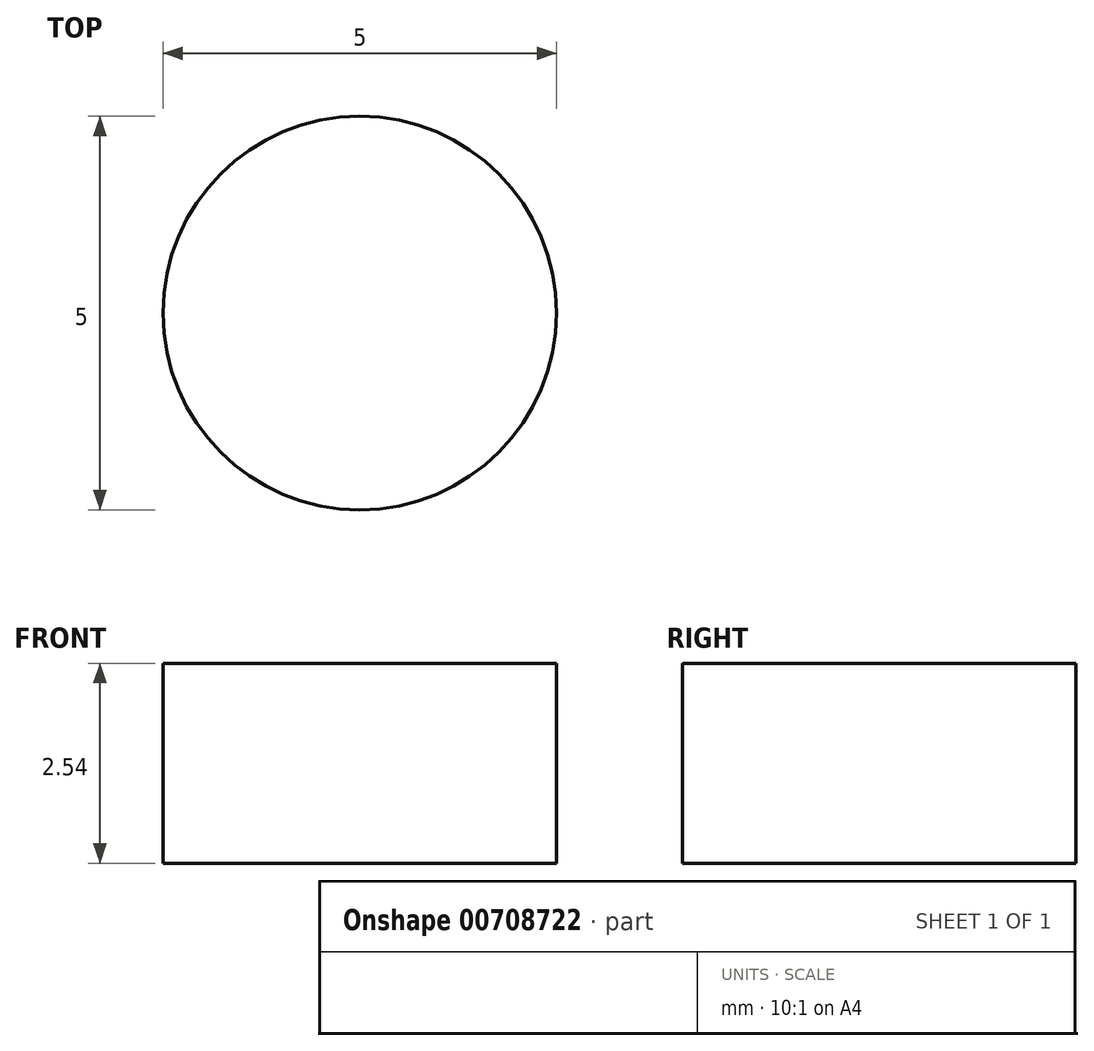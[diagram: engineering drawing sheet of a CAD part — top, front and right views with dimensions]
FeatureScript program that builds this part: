
annotation { "Feature Type Name" : "Feature", "Feature Type Description" : "" }
export const myFeature = defineFeature(function(context is Context, id is Id, definition is map)
    precondition{}
    {
        {
            var Q0;
            Q0=qCreatedBy(makeId("Top.planeOp"),FACE);
            var sketch = newSketch(context, id + "F0", { "sketchPlane" : qUnion([Q0])});
            skCircle(sketch, "E0", {"center": v(0, 0) * mm, "radius": 2.5 * mm});
            skSolve(sketch);
        }
        {
            var Q0;
            Q0=makeQuery(id+"F0.imprint","IMPRINT",FACE,{"disambiguationData":[TD([[makeQuery(id+"F0.imprint","IMPRINT",EDGE,{"derivedFrom":sQuery(id+"F0.wireOp",EDGE,"E0")}),1.0]])]});
            extrude(context, id + "F1", {"entities" : qUnion([Q0]), "depth" : 2.54 * mm, "offsetDistance" : 25.4 * mm});
        }
    });
